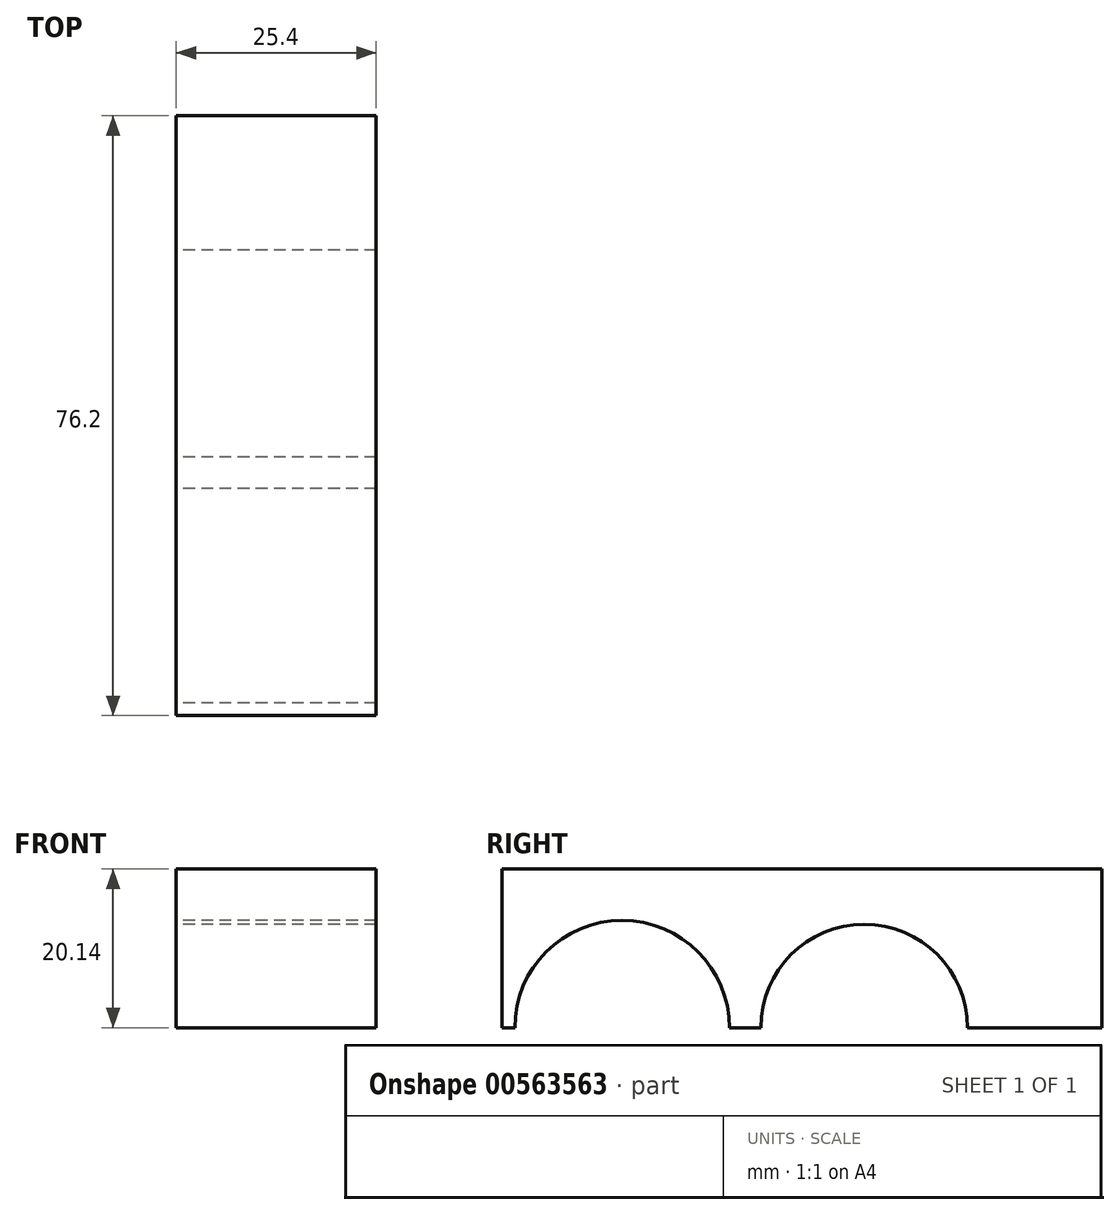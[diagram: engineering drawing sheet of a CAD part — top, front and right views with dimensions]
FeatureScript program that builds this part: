
annotation { "Feature Type Name" : "Feature", "Feature Type Description" : "" }
export const myFeature = defineFeature(function(context is Context, id is Id, definition is map)
    precondition{}
    {
        {
            var Q0;
            Q0=qCreatedBy(makeId("Right.planeOp"),FACE);
            var sketch = newSketch(context, id + "F0", { "sketchPlane" : qUnion([Q0])});
            skLineSegment(sketch, "E0.bottom", {"start": v(-101.5, 52.36) * mm, "end": v(101.7, 52.36) * mm});
            skLineSegment(sketch, "E0.top", {"start": v(-101.5, -55.52) * mm, "end": v(101.7, -55.52) * mm});
            skLineSegment(sketch, "E0.left", {"start": v(-101.5, 52.36) * mm, "end": v(-101.5, -55.52) * mm});
            skLineSegment(sketch, "E0.right", {"start": v(101.7, 52.36) * mm, "end": v(101.7, -55.52) * mm});
            skLineSegment(sketch, "E1.bottom", {"start": v(-31.84, -35.38) * mm, "end": v(44.36, -35.38) * mm});
            skLineSegment(sketch, "E1.top", {"start": v(-31.84, -55.52) * mm, "end": v(44.36, -55.52) * mm});
            skLineSegment(sketch, "E1.left", {"start": v(-31.84, -35.38) * mm, "end": v(-31.84, -55.52) * mm});
            skLineSegment(sketch, "E1.right", {"start": v(44.36, -35.38) * mm, "end": v(44.36, -55.52) * mm});
            skCircle(sketch, "E2", {"center": v(-16.6, -55.52) * mm, "radius": 13.63 * mm});
            skCircle(sketch, "E3", {"center": v(14.15, -55.52) * mm, "radius": 13.14 * mm});
            skSolve(sketch);
        }
        {
            var Q0;
            {var subQ0=sQuery(id+"F0.wireOp",EDGE,"E2");var subQ1=sQuery(id+"F0.wireOp",EDGE,"E1.top");var subQ2=makeQuery(id+"F0.imprint","INTERSECT",VERTEX,{"disambiguationData":[OD(0.0)],"derivedFrom":[subQ1,subQ0]});Q0=makeQuery(id+"F0.imprint","IMPRINT",FACE,{"disambiguationData":[TD([[makeQuery(id+"F0.imprint","IMPRINT",EDGE,{"disambiguationData":[TD([[subQ2,-1.0]])],"derivedFrom":subQ1}),-1.0]])]});}
            var Q1;
            {var subQ0=sQuery(id+"F0.wireOp",EDGE,"E3");var subQ1=sQuery(id+"F0.wireOp",EDGE,"E1.top");var subQ2=makeQuery(id+"F0.imprint","INTERSECT",VERTEX,{"disambiguationData":[OD(0.0)],"derivedFrom":[subQ1,subQ0]});Q1=makeQuery(id+"F0.imprint","IMPRINT",FACE,{"disambiguationData":[TD([[makeQuery(id+"F0.imprint","IMPRINT",EDGE,{"disambiguationData":[TD([[subQ2,-1.0]])],"derivedFrom":subQ1}),-1.0]])]});}
            var Q2;
            {var subQ0=sQuery(id+"F0.wireOp",EDGE,"E2");var subQ1=sQuery(id+"F0.wireOp",EDGE,"E1.top");var subQ2=makeQuery(id+"F0.imprint","INTERSECT",VERTEX,{"disambiguationData":[OD(0.0)],"derivedFrom":[subQ1,subQ0]});Q2=makeQuery(id+"F0.imprint","IMPRINT",FACE,{"disambiguationData":[TD([[makeQuery(id+"F0.imprint","IMPRINT",EDGE,{"disambiguationData":[TD([[subQ2,-1.0]])],"derivedFrom":subQ1}),1.0]])]});}
            var Q3;
            {var subQ0=sQuery(id+"F0.wireOp",EDGE,"E3");var subQ1=sQuery(id+"F0.wireOp",EDGE,"E1.top");var subQ2=makeQuery(id+"F0.imprint","INTERSECT",VERTEX,{"disambiguationData":[OD(0.0)],"derivedFrom":[subQ1,subQ0]});Q3=makeQuery(id+"F0.imprint","IMPRINT",FACE,{"disambiguationData":[TD([[makeQuery(id+"F0.imprint","IMPRINT",EDGE,{"disambiguationData":[TD([[subQ2,-1.0]])],"derivedFrom":subQ1}),1.0]])]});}
            var Q4;
            Q4=makeQuery(id+"F0.imprint","IMPRINT",FACE,{"disambiguationData":[TD([[makeQuery(id+"F0.imprint","IMPRINT",EDGE,{"derivedFrom":sQuery(id+"F0.wireOp",EDGE,"E1.bottom")}),-1.0]])]});
            extrude(context, id + "F1", {"entities" : qUnion([Q0, Q1, Q2, Q3, Q4]), "depth" : 25.4 * mm, "offsetDistance" : 25.4 * mm});
        }
    });
